# Revit family: Electronics_Interfaces_Biamp_Vocia_Control_CI-1__
name_source: partatom
category: Communication Devices
units: mm (PartAtom-declared; Revit-internal decimal feet)

## family parameters
Cut with Voids When Loaded = No
Host = Face
Maintain Annotation Orientation = No
OmniClass Number = 23.85.10.11.11
OmniClass Title = Sound and Signal Devices
Part Type = Normal
Room Calculation Point = No
Round Connector Dimension = Use Diameter
Shared = No

## types (1)
- CI-1
    Altitude = 0-10,000 ft (0-3000m) MSL
    Apparent Load = 30 VA
    Assertion Alarm Inputs = Transition from 0V to 12-24V
    Assertion Fault Inputs = Transition from +V to 0V
    Assertion Outputs = Low
    Compliance = EN 54-16 certified, CE marked (Europe), RINA (Italy), RoHS Directive (Europe), EN 60849, AS 60849 verified
    Connector Description = Dual 24V DC, 15W each
    Current Limit = 800mA
    Default Elevation = 48 "
    Depth = 10 "
    Description = Vocia® CI-1 Control Interface
    Height = 1.75 "
    Housing Material = Biamp - Metal - Silver
    Humidity = 0-100% relative humidity (non-condensing)
    Manufacturer = Biamp
    Max Continuous Current = 350mA
    Max Power Consumption = 30 W
    Maximum External Supply = 35V
    Maximum pull-up resistor = 2.2 kohm
    Model = Vocia CI-1
    Number of Poles = 1
    Power Factor = 1
    Product Documentation Link = https://downloads.biamp.com
    Product Page URL = https://www.biamp.com
    Product data url = https://www.bimobject.com
    Pull-up Load = max 2.2 kohm
    Temperature Range = 32 - 113° F (0 - 45° C)
    URL = https://www.biamp.com
    Vocia CI-1 = Yes
    Voltage = 24 V
    Weight = 6.40 lbf
    Width = 19 "

## geometry (parser evidence)
native form markers: Sweep x2
no freeform markers — native parametric forms only
